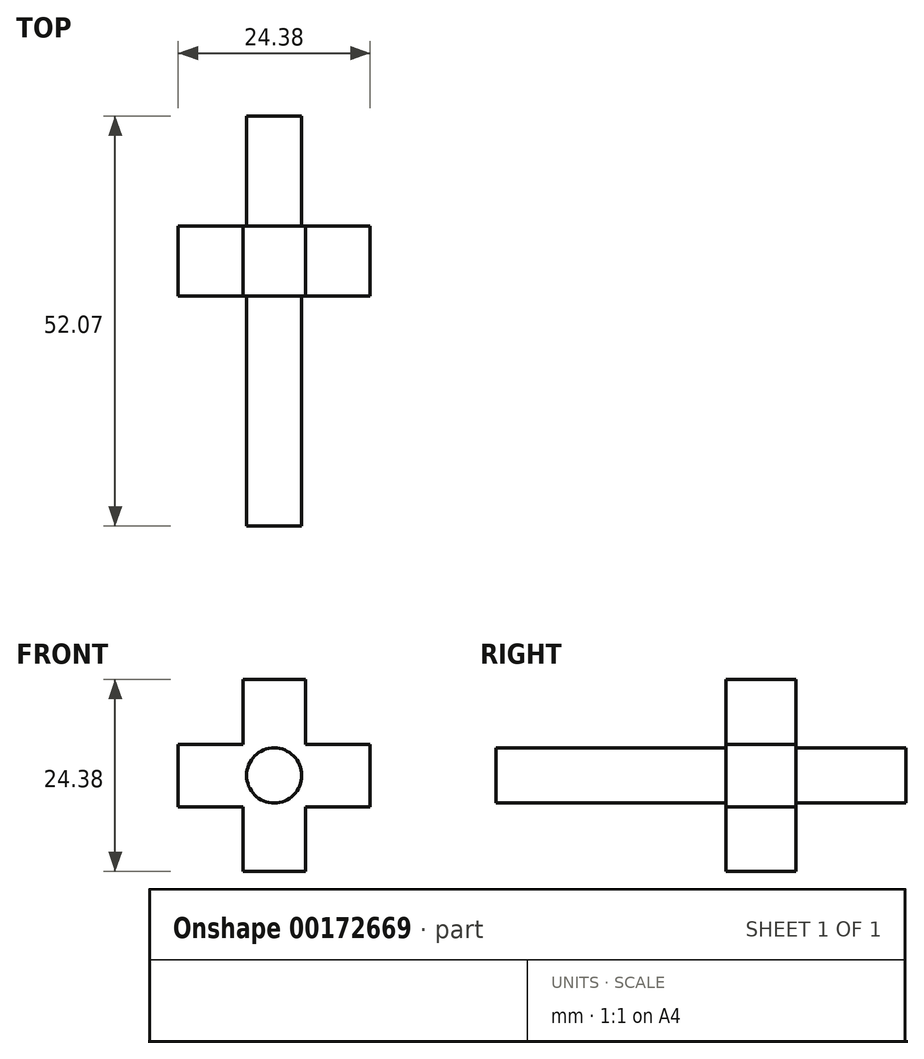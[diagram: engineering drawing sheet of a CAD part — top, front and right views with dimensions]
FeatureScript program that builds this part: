
annotation { "Feature Type Name" : "Feature", "Feature Type Description" : "" }
export const myFeature = defineFeature(function(context is Context, id is Id, definition is map)
    precondition{}
    {
        {
            var Q0;
            Q0=qCreatedBy(makeId("Front.planeOp"),FACE);
            var sketch = newSketch(context, id + "F0", { "sketchPlane" : qUnion([Q0])});
            skLineSegment(sketch, "E0.bottom", {"start": v(12.2, 3.97) * mm, "end": v(3.97, 3.97) * mm});
            skLineSegment(sketch, "E0.top", {"start": v(12.2, -3.97) * mm, "end": v(3.97, -3.97) * mm});
            skLineSegment(sketch, "E0.left", {"start": v(12.2, 3.97) * mm, "end": v(12.2, -3.97) * mm});
            skLineSegment(sketch, "E0.right", {"start": v(-12.2, 3.97) * mm, "end": v(-12.2, -3.97) * mm});
            skPoint(sketch, "E0.middle", {"position": v(0, 0) * mm});
            skLineSegment(sketch, "E1.bottom", {"start": v(3.97, 12.2) * mm, "end": v(-3.97, 12.2) * mm});
            skLineSegment(sketch, "E1.top", {"start": v(3.97, -12.2) * mm, "end": v(-3.97, -12.2) * mm});
            skLineSegment(sketch, "E1.left", {"start": v(3.97, 12.2) * mm, "end": v(3.97, 3.97) * mm});
            skLineSegment(sketch, "E1.right", {"start": v(-3.97, 12.2) * mm, "end": v(-3.97, 3.97) * mm});
            skCircle(sketch, "E2", {"center": v(0, 0) * mm, "radius": 3.5 * mm});
            skLineSegment(sketch, "E3.trimOffspring", {"start": v(-3.97, 3.97) * mm, "end": v(-12.2, 3.97) * mm});
            skLineSegment(sketch, "E4.trimOffspring", {"start": v(-3.97, -3.97) * mm, "end": v(-3.97, -12.2) * mm});
            skLineSegment(sketch, "E5.trimOffspring", {"start": v(-3.97, -3.97) * mm, "end": v(-12.2, -3.97) * mm});
            skLineSegment(sketch, "E6.trimOffspring", {"start": v(3.97, -3.97) * mm, "end": v(3.97, -12.2) * mm});
            skSolve(sketch);
        }
        {
            var Q0;
            Q0=makeQuery(id+"F0.imprint","IMPRINT",FACE,{"disambiguationData":[TD([[makeQuery(id+"F0.imprint","IMPRINT",EDGE,{"derivedFrom":sQuery(id+"F0.wireOp",EDGE,"E0.bottom")}),1.0]])]});
            extrude(context, id + "F1", {"entities" : qUnion([Q0]), "depth" : 8.9 * mm});
        }
        {
            var Q0;
            Q0=makeQuery(id+"F0.imprint","IMPRINT",FACE,{"disambiguationData":[TD([[makeQuery(id+"F0.imprint","IMPRINT",EDGE,{"derivedFrom":sQuery(id+"F0.wireOp",EDGE,"E2")}),1.0]])]});
            extrude(context, id + "F2", {"entities" : qUnion([Q0]), "operationType" : NewBodyOperationType.ADD, "depth" : 38.1 * mm});
        }
        {
            var Q0;
            Q0=makeQuery(id+"F0.imprint","IMPRINT",FACE,{"disambiguationData":[TD([[makeQuery(id+"F0.imprint","IMPRINT",EDGE,{"derivedFrom":sQuery(id+"F0.wireOp",EDGE,"E2")}),1.0]])]});
            extrude(context, id + "F3", {"entities" : qUnion([Q0]), "operationType" : NewBodyOperationType.ADD, "oppositeDirection" : true, "depth" : 13.97 * mm});
        }
    });
